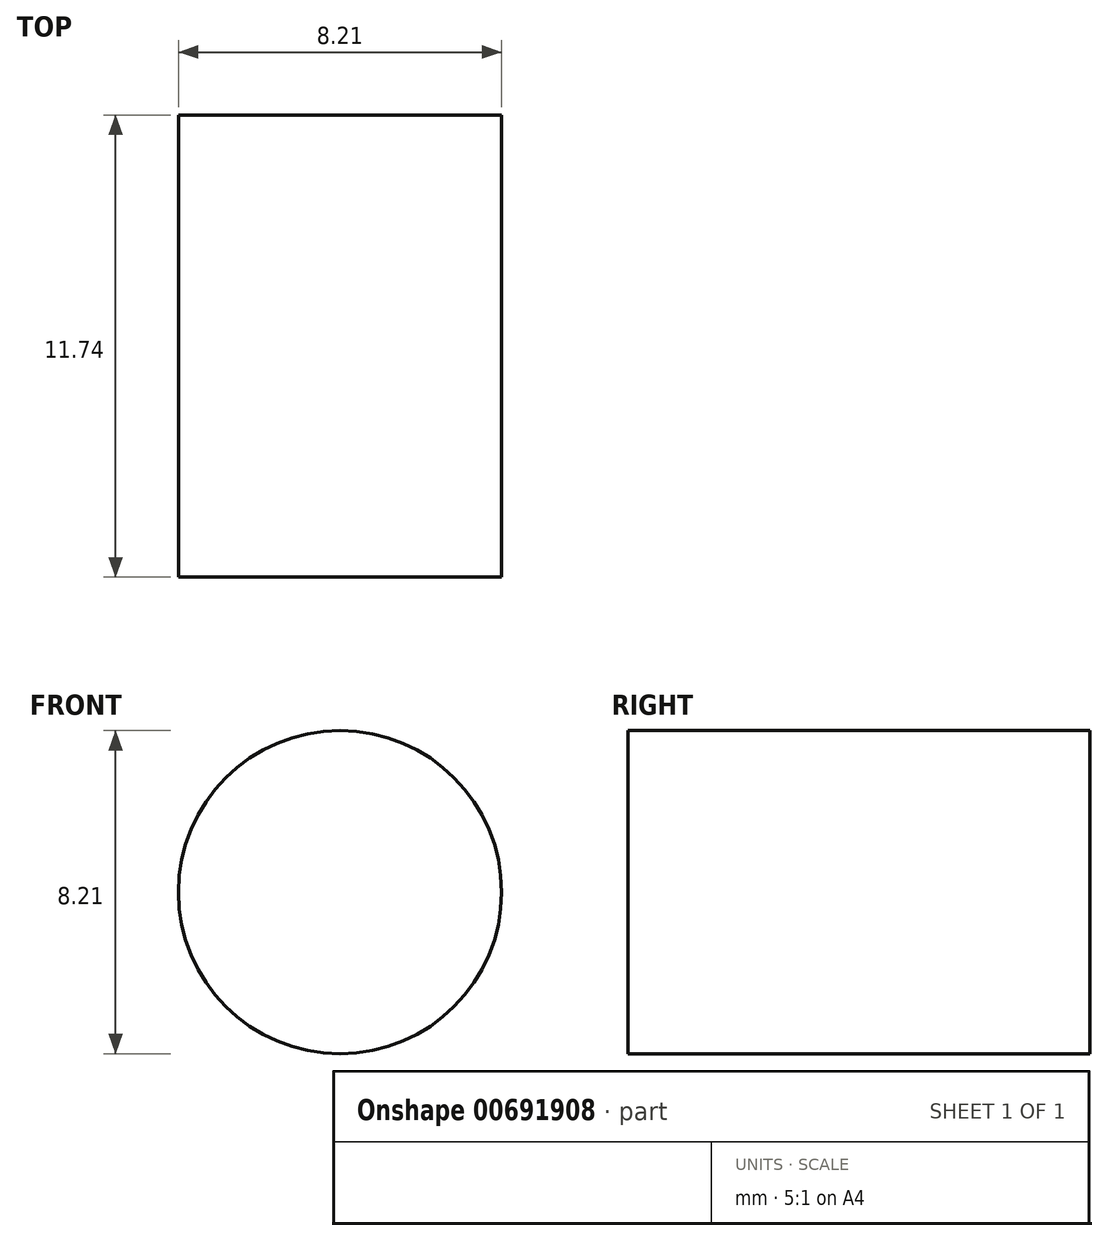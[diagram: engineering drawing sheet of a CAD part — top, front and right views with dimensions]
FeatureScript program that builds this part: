
annotation { "Feature Type Name" : "Feature", "Feature Type Description" : "" }
export const myFeature = defineFeature(function(context is Context, id is Id, definition is map)
    precondition{}
    {
        {
            var Q0;
            Q0=qCreatedBy(makeId("Front.planeOp"),FACE);
            var sketch = newSketch(context, id + "F0", { "sketchPlane" : qUnion([Q0])});
            skCircle(sketch, "E0", {"center": v(-37.7, 31.44) * mm, "radius": 4.1 * mm});
            skSolve(sketch);
        }
        {
            var Q0;
            Q0 = qSketchRegion(id + "F0", true);
            var Q1;
            Q1=makeQuery(id+"F0.imprint","IMPRINT",FACE,{"disambiguationData":[TD([[makeQuery(id+"F0.imprint","IMPRINT",EDGE,{"derivedFrom":sQuery(id+"F0.wireOp",EDGE,"E0")}),1.0]])]});
            extrude(context, id + "F1", {"entities" : qUnion([Q0, Q1]), "depth" : 11.74 * mm, "offsetDistance" : 25.4 * mm});
        }
    });
